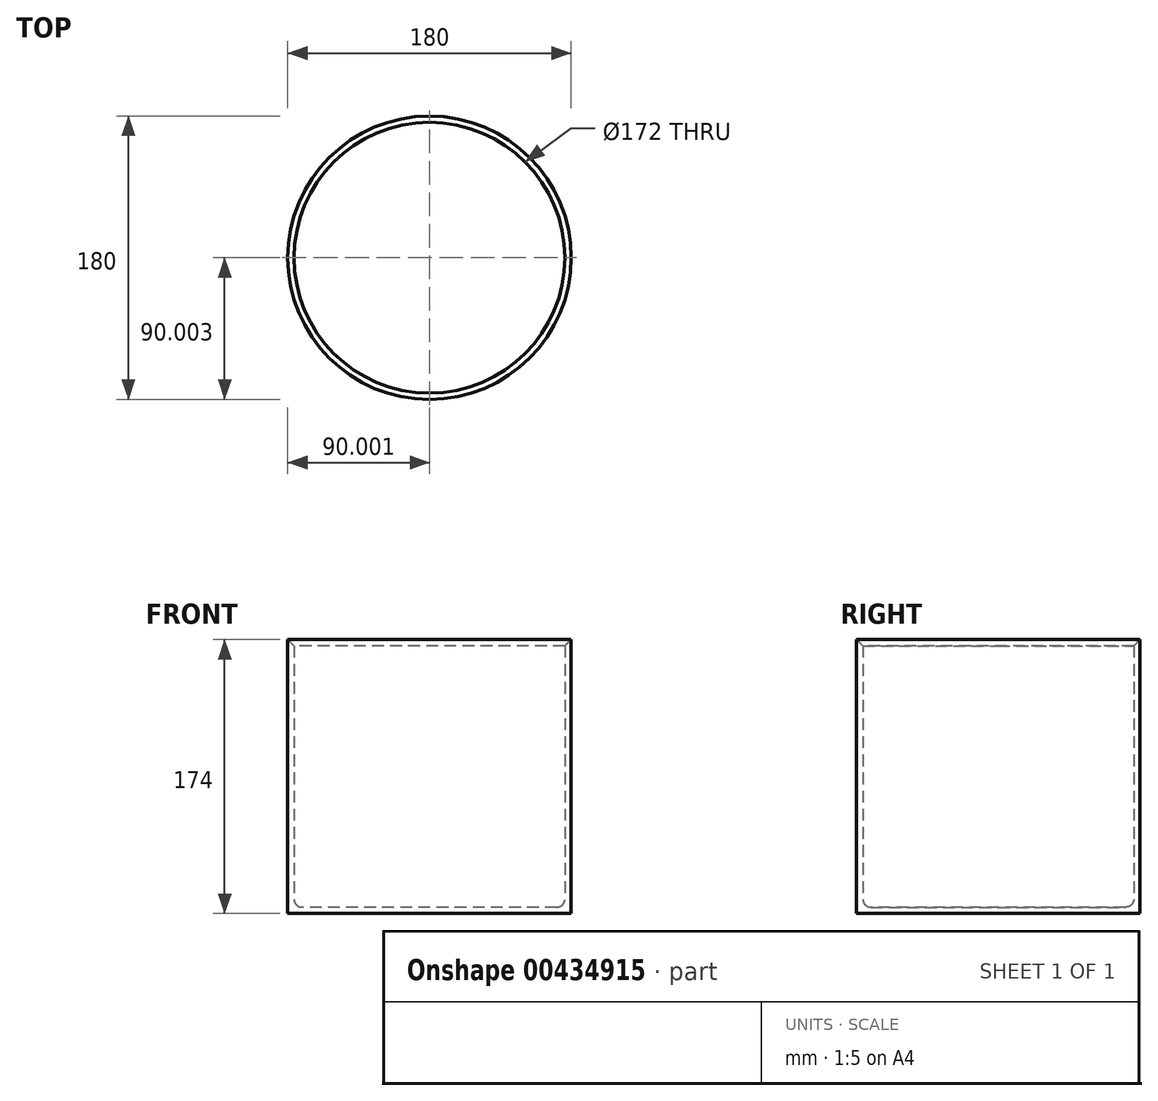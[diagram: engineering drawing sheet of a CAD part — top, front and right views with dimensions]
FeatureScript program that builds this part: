
annotation { "Feature Type Name" : "Feature", "Feature Type Description" : "" }
export const myFeature = defineFeature(function(context is Context, id is Id, definition is map)
    precondition{}
    {
        {
            var Q0;
            Q0=qCreatedBy(makeId("Top.planeOp"),FACE);
            var sketch = newSketch(context, id + "F0", { "sketchPlane" : qUnion([Q0])});
            skCircle(sketch, "E0", {"center": v(-3.39, 2.33) * mm, "radius": 90 * mm});
            skSolve(sketch);
        }
        {
            var Q0;
            Q0=makeQuery(id+"F0.imprint","IMPRINT",FACE,{"disambiguationData":[TD([[makeQuery(id+"F0.imprint","IMPRINT",EDGE,{"derivedFrom":sQuery(id+"F0.wireOp",EDGE,"E0")}),1.0]])]});
            extrude(context, id + "F1", {"entities" : qUnion([Q0]), "depth" : 4 * mm});
        }
        {
            var Q0;
            Q0=makeQuery(id+"F1.opExtrude","CAP_FACE",FACE,{"disambiguationData":[OSD([sQuery(id+"F0.wireOp",EDGE,"E0")])],"isStart":false});
            var sketch = newSketch(context, id + "F2", { "sketchPlane" : qUnion([Q0])});
            skCircle(sketch, "E1.0", {"center": v(-3.39, 2.33) * mm, "radius": 86 * mm});
            skSolve(sketch);
        }
        {
            var Q0;
            Q0=makeQuery(id+"F2.imprint","IMPRINT",FACE,{"disambiguationData":[TD([[makeQuery(id+"F2.imprint","IMPRINT",EDGE,{"derivedFrom":sQuery(id+"F2.wireOp",EDGE,"E1.0")}),-1.0]])]});
            extrude(context, id + "F3", {"entities" : qUnion([Q0]), "operationType" : NewBodyOperationType.ADD, "depth" : 170 * mm});
        }
        {
            var Q0;
            Q0=makeQuery(id+"F1.opExtrude","CAP_FACE",FACE,{"disambiguationData":[OSD([sQuery(id+"F0.wireOp",EDGE,"E0")])],"isStart":false});
            fillet(context, id + "F4", {"entities" : qUnion([Q0]), "radius" : 5 * mm, "tangentPropagation" : true, "allowEdgeOverflow" : false});
        }
        {
            var Q0;
            Q0=makeQuery(id+"F3.opExtrude","CAP_EDGE",EDGE,{"disambiguationData":[OSD([sQuery(id+"F2.wireOp",EDGE,"E1.0")])],"isStart":false});
            chamfer(context, id + "F5", {"entities" : qUnion([Q0]), "width" : 4 * mm, "tangentPropagation" : true});
        }
    });
